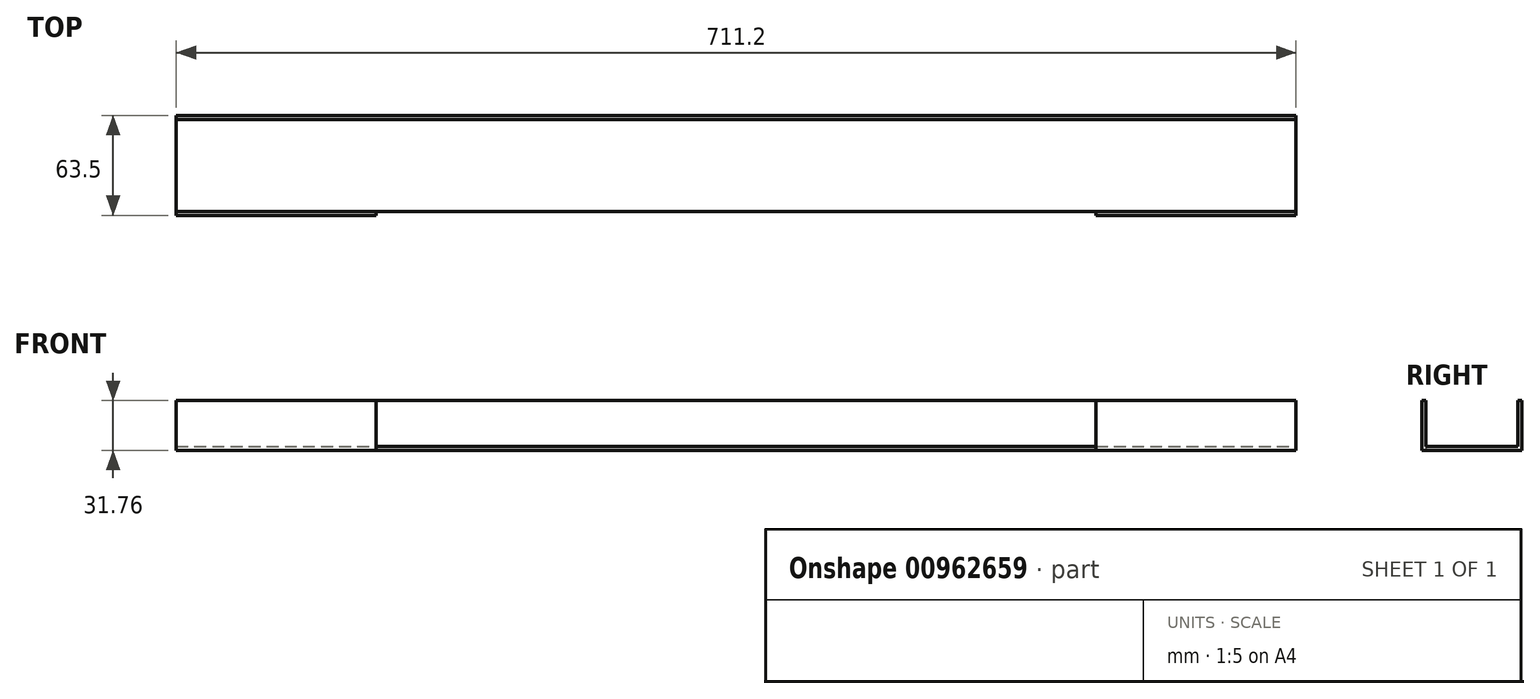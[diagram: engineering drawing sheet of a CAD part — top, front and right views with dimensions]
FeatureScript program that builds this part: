
annotation { "Feature Type Name" : "Feature", "Feature Type Description" : "" }
export const myFeature = defineFeature(function(context is Context, id is Id, definition is map)
    precondition{}
    {
        {
            var Q0;
            Q0=qCreatedBy(makeId("Front.planeOp"),FACE);
            var sketch = newSketch(context, id + "F0", { "sketchPlane" : qUnion([Q0])});
            skLineSegment(sketch, "E0.bottom", {"start": v(-355.6, 15.88) * mm, "end": v(355.6, 15.88) * mm});
            skLineSegment(sketch, "E0.top", {"start": v(-355.6, -15.88) * mm, "end": v(355.6, -15.88) * mm});
            skLineSegment(sketch, "E0.left", {"start": v(-355.6, 15.88) * mm, "end": v(-355.6, -15.88) * mm});
            skLineSegment(sketch, "E0.right", {"start": v(355.6, 15.88) * mm, "end": v(355.6, -15.88) * mm});
            skPoint(sketch, "E0.middle", {"position": v(0, 0) * mm});
            skSolve(sketch);
        }
        {
            var Q0;
            Q0=makeQuery(id+"F0.imprint","IMPRINT",FACE,{"disambiguationData":[TD([[makeQuery(id+"F0.imprint","IMPRINT",EDGE,{"derivedFrom":sQuery(id+"F0.wireOp",EDGE,"E0.bottom")}),-1.0]])]});
            extrude(context, id + "F1", {"entities" : qUnion([Q0]), "depth" : 63.5 * mm, "offsetDistance" : 25.4 * mm});
        }
        {
            var Q0;
            Q0=makeQuery(id+"F1.opExtrude","SWEPT_FACE",FACE,{"disambiguationData":[OSD([sQuery(id+"F0.wireOp",EDGE,"E0.right")])]});
            var sketch = newSketch(context, id + "F2", { "sketchPlane" : qUnion([Q0])});
            skLineSegment(sketch, "E1", {"start": v(-60.96, 15.88) * mm, "end": v(-60.96, -13.33) * mm});
            skLineSegment(sketch, "E2", {"start": v(-60.96, -13.33) * mm, "end": v(-2.54, -13.33) * mm});
            skLineSegment(sketch, "E3", {"start": v(-2.54, -13.33) * mm, "end": v(-2.54, 15.88) * mm});
            skSolve(sketch);
        }
        {
            var Q0;
            Q0 = qSketchRegion(id + "F2", true);
            var Q1;
            {var subQ0=sQuery(id+"F2.wireOp",EDGE,"E1");Q1=makeQuery(id+"F2.imprint","IMPRINT",FACE,{"disambiguationData":[TD([[makeQuery(id+"F2.imprint","IMPRINT",EDGE,{"derivedFrom":subQ0}),1.0]])]});}
            extrude(context, id + "F3", {"entities" : qUnion([Q0, Q1]), "operationType" : NewBodyOperationType.REMOVE, "endBound" : BoundingType.THROUGH_ALL, "oppositeDirection" : true, "depth" : 25.4 * mm, "offsetDistance" : 25.4 * mm});
        }
        {
            var Q0;
            Q0=makeQuery(id+"F1.opExtrude","CAP_FACE",FACE,{"disambiguationData":[OSD([sQuery(id+"F0.wireOp",EDGE,"E0.bottom"),sQuery(id+"F0.wireOp",EDGE,"E0.top"),sQuery(id+"F0.wireOp",EDGE,"E0.left"),sQuery(id+"F0.wireOp",EDGE,"E0.right")])],"isStart":false});
            var sketch = newSketch(context, id + "F4", { "sketchPlane" : qUnion([Q0])});
            skLineSegment(sketch, "E4.bottom", {"start": v(-228.6, 15.88) * mm, "end": v(228.6, 15.88) * mm});
            skLineSegment(sketch, "E4.top", {"start": v(-228.6, -15.88) * mm, "end": v(228.6, -15.88) * mm});
            skLineSegment(sketch, "E4.left", {"start": v(-228.6, 15.88) * mm, "end": v(-228.6, -15.88) * mm});
            skLineSegment(sketch, "E4.right", {"start": v(228.6, 15.88) * mm, "end": v(228.6, -15.88) * mm});
            skSolve(sketch);
        }
        {
            var Q0;
            Q0=makeQuery(id+"F4.imprint","IMPRINT",FACE,{"disambiguationData":[TD([[makeQuery(id+"F4.imprint","IMPRINT",EDGE,{"derivedFrom":sQuery(id+"F4.wireOp",EDGE,"E4.bottom")}),-1.0]])]});
            extrude(context, id + "F5", {"entities" : qUnion([Q0]), "operationType" : NewBodyOperationType.REMOVE, "oppositeDirection" : true, "depth" : 2.54 * mm, "offsetDistance" : 25.4 * mm});
        }
    });
